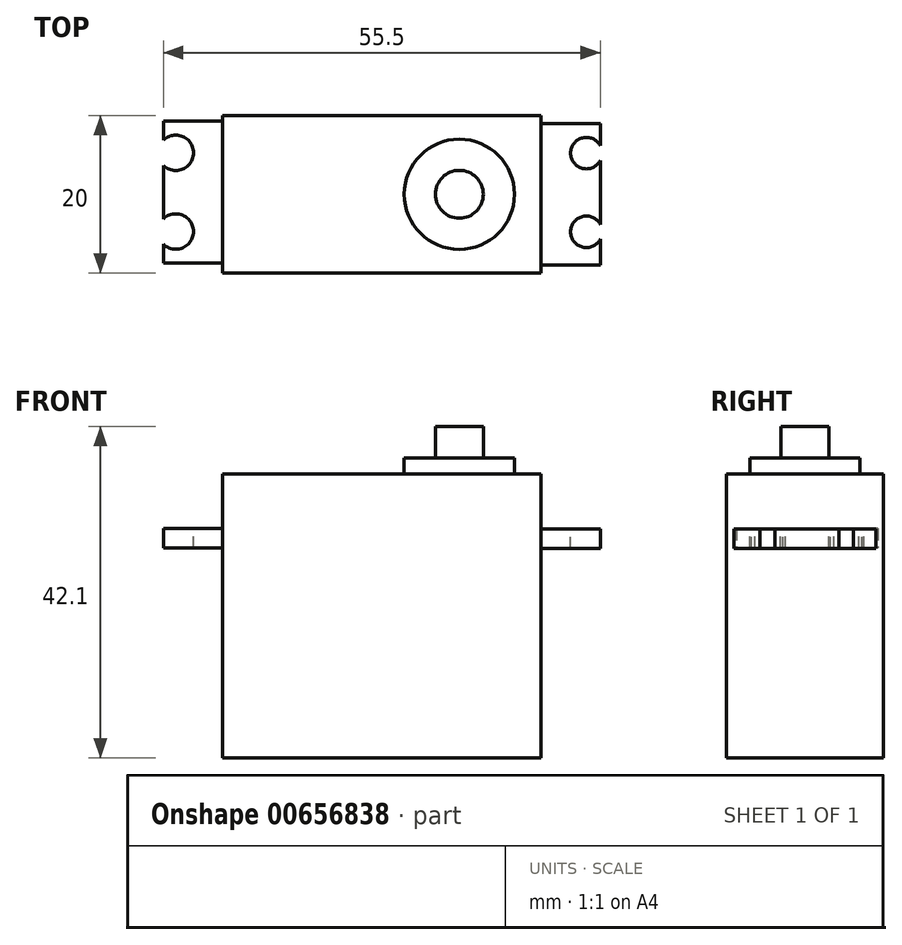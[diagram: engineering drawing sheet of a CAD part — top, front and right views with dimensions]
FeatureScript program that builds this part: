
annotation { "Feature Type Name" : "Feature", "Feature Type Description" : "" }
export const myFeature = defineFeature(function(context is Context, id is Id, definition is map)
    precondition{}
    {
        {
            var Q0;
            Q0=qCreatedBy(makeId("Top.planeOp"),FACE);
            var sketch = newSketch(context, id + "F0", { "sketchPlane" : qUnion([Q0])});
            skLineSegment(sketch, "E0.bottom", {"start": v(-74.66, 58.2) * mm, "end": v(-34.16, 58.2) * mm});
            skLineSegment(sketch, "E0.top", {"start": v(-74.66, 38.2) * mm, "end": v(-34.16, 38.2) * mm});
            skLineSegment(sketch, "E0.left", {"start": v(-74.66, 58.2) * mm, "end": v(-74.66, 38.2) * mm});
            skLineSegment(sketch, "E0.right", {"start": v(-34.16, 58.2) * mm, "end": v(-34.16, 38.2) * mm});
            skSolve(sketch);
        }
        {
            var Q0;
            Q0 = qSketchRegion(id + "F0", true);
            extrude(context, id + "F1", {"entities" : qUnion([Q0]), "depth" : 36.1 * mm, "offsetDistance" : 25 * mm});
        }
        {
            var Q0;
            Q0=makeQuery(id+"F1.opExtrude","SWEPT_FACE",FACE,{"disambiguationData":[OSD([sQuery(id+"F0.wireOp",EDGE,"E0.right")])]});
            var sketch = newSketch(context, id + "F2", { "sketchPlane" : qUnion([Q0])});
            skLineSegment(sketch, "E1.bottom", {"start": v(39.2, 29.1) * mm, "end": v(57.2, 29.1) * mm});
            skLineSegment(sketch, "E1.top", {"start": v(39.2, 26.6) * mm, "end": v(57.2, 26.6) * mm});
            skLineSegment(sketch, "E1.left", {"start": v(39.2, 29.1) * mm, "end": v(39.2, 26.6) * mm});
            skLineSegment(sketch, "E1.right", {"start": v(57.2, 29.1) * mm, "end": v(57.2, 26.6) * mm});
            skLineSegment(sketch, "E2", {"start": v(48.2, 36.1) * mm, "end": v(48.2, 29.1) * mm, "construction": true});
            skSolve(sketch);
        }
        {
            var Q0;
            Q0=makeQuery(id+"F2.imprint","IMPRINT",FACE,{"disambiguationData":[TD([[makeQuery(id+"F2.imprint","IMPRINT",EDGE,{"derivedFrom":sQuery(id+"F2.wireOp",EDGE,"E1.bottom")}),-1.0]])]});
            extrude(context, id + "F3", {"entities" : qUnion([Q0]), "operationType" : NewBodyOperationType.ADD, "depth" : 7.5 * mm, "offsetDistance" : 25 * mm});
        }
        {
            var Q0;
            Q0=makeQuery(id+"F1.opExtrude","SWEPT_FACE",FACE,{"disambiguationData":[OSD([sQuery(id+"F0.wireOp",EDGE,"E0.left")])]});
            var sketch = newSketch(context, id + "F4", { "sketchPlane" : qUnion([Q0])});
            skLineSegment(sketch, "E3.bottom", {"start": v(-57.47, 29.15) * mm, "end": v(-39.47, 29.15) * mm});
            skLineSegment(sketch, "E3.top", {"start": v(-57.47, 26.65) * mm, "end": v(-39.47, 26.65) * mm});
            skLineSegment(sketch, "E3.left", {"start": v(-57.47, 29.15) * mm, "end": v(-57.47, 26.65) * mm});
            skLineSegment(sketch, "E3.right", {"start": v(-39.47, 29.15) * mm, "end": v(-39.47, 26.65) * mm});
            skSolve(sketch);
        }
        {
            var Q0;
            Q0 = qSketchRegion(id + "F4", true);
            extrude(context, id + "F5", {"entities" : qUnion([Q0]), "operationType" : NewBodyOperationType.ADD, "depth" : 7.5 * mm, "offsetDistance" : 25 * mm});
        }
        {
            var Q0;
            Q0=makeQuery(id+"F1.opExtrude","CAP_FACE",FACE,{"disambiguationData":[OSD([sQuery(id+"F0.wireOp",EDGE,"E0.bottom"),sQuery(id+"F0.wireOp",EDGE,"E0.top"),sQuery(id+"F0.wireOp",EDGE,"E0.left"),sQuery(id+"F0.wireOp",EDGE,"E0.right")])],"isStart":false});
            var sketch = newSketch(context, id + "F6", { "sketchPlane" : qUnion([Q0])});
            skCircle(sketch, "E4", {"center": v(-44.56, 48.2) * mm, "radius": 7 * mm});
            skLineSegment(sketch, "E5", {"start": v(-44.56, 48.2) * mm, "end": v(-34.16, 48.2) * mm, "construction": true});
            skSolve(sketch);
        }
        {
            var Q0;
            Q0 = qSketchRegion(id + "F6", true);
            extrude(context, id + "F7", {"entities" : qUnion([Q0]), "operationType" : NewBodyOperationType.ADD, "depth" : 2 * mm, "offsetDistance" : 25 * mm});
        }
        {
            var Q0;
            Q0=makeQuery(id+"F7.opExtrude","CAP_FACE",FACE,{"disambiguationData":[OSD([sQuery(id+"F6.wireOp",EDGE,"E4")])],"isStart":false});
            var sketch = newSketch(context, id + "F8", { "sketchPlane" : qUnion([Q0])});
            skCircle(sketch, "E6", {"center": v(-44.56, 48.2) * mm, "radius": 3.04 * mm});
            skSolve(sketch);
        }
        {
            var Q0;
            Q0=makeQuery(id+"F8.imprint","IMPRINT",FACE,{"disambiguationData":[TD([[makeQuery(id+"F8.imprint","IMPRINT",EDGE,{"derivedFrom":sQuery(id+"F8.wireOp",EDGE,"E6")}),1.0]])]});
            var sketch = newSketch(context, id + "F9", { "sketchPlane" : qUnion([Q0])});
            skSolve(sketch);
        }
        {
            var Q0;
            Q0=makeQuery(id+"F9.imprint","IMPRINT",FACE,{"disambiguationData":[TD([[makeQuery(id+"F9.imprint","IMPRINT",EDGE,{"derivedFrom":makeQuery(id+"F8.imprint","IMPRINT",EDGE,{"derivedFrom":sQuery(id+"F8.wireOp",EDGE,"E6")})}),1.0]])]});
            extrude(context, id + "F10", {"entities" : qUnion([Q0]), "operationType" : NewBodyOperationType.ADD, "depth" : 4 * mm, "offsetDistance" : 25 * mm});
        }
        {
            var Q0;
            Q0=makeQuery(id+"F5.opExtrude","SWEPT_FACE",FACE,{"disambiguationData":[OSD([sQuery(id+"F4.wireOp",EDGE,"E3.bottom")])]});
            var sketch = newSketch(context, id + "F11", { "sketchPlane" : qUnion([Q0])});
            skCircle(sketch, "E7", {"center": v(-80.58, 53.47) * mm, "radius": 2.25 * mm});
            skCircle(sketch, "E8", {"center": v(-80.58, 43.47) * mm, "radius": 2.25 * mm});
            skLineSegment(sketch, "E9", {"start": v(-80.58, 53.47) * mm, "end": v(-80.58, 43.47) * mm, "construction": true});
            skLineSegment(sketch, "E10", {"start": v(-80.58, 48.47) * mm, "end": v(-74.66, 48.47) * mm, "construction": true});
            skSolve(sketch);
        }
        {
            var Q0;
            {var subQ0=sQuery(id+"F11.wireOp",EDGE,"E7");var subQ1=makeQuery(id+"F5.opExtrude","CAP_EDGE",EDGE,{"disambiguationData":[OSD([sQuery(id+"F4.wireOp",EDGE,"E3.bottom")])],"isStart":false});var subQ2=makeQuery(id+"F11.imprint","INTERSECT",VERTEX,{"disambiguationData":[OD(0.0)],"derivedFrom":[subQ1,subQ0]});Q0=makeQuery(id+"F11.imprint","IMPRINT",FACE,{"disambiguationData":[TD([[makeQuery(id+"F11.imprint","IMPRINT",EDGE,{"disambiguationData":[TD([[subQ2,1.0]])],"derivedFrom":subQ0}),1.0]])]});}
            var Q1;
            {var subQ0=sQuery(id+"F11.wireOp",EDGE,"E8");var subQ1=makeQuery(id+"F5.opExtrude","CAP_EDGE",EDGE,{"disambiguationData":[OSD([sQuery(id+"F4.wireOp",EDGE,"E3.bottom")])],"isStart":false});var subQ2=makeQuery(id+"F11.imprint","INTERSECT",VERTEX,{"disambiguationData":[OD(0.0)],"derivedFrom":[subQ1,subQ0]});Q1=makeQuery(id+"F11.imprint","IMPRINT",FACE,{"disambiguationData":[TD([[makeQuery(id+"F11.imprint","IMPRINT",EDGE,{"disambiguationData":[TD([[subQ2,-1.0]])],"derivedFrom":subQ0}),1.0]])]});}
            extrude(context, id + "F12", {"entities" : qUnion([Q0, Q1]), "operationType" : NewBodyOperationType.REMOVE, "oppositeDirection" : true, "depth" : 3 * mm, "offsetDistance" : 25 * mm});
        }
        {
            var Q0;
            Q0=makeQuery(id+"F3.opExtrude","SWEPT_FACE",FACE,{"disambiguationData":[OSD([sQuery(id+"F2.wireOp",EDGE,"E1.bottom")])]});
            var sketch = newSketch(context, id + "F13", { "sketchPlane" : qUnion([Q0])});
            skCircle(sketch, "E11", {"center": v(-28.42, 53.43) * mm, "radius": 2 * mm});
            skCircle(sketch, "E12", {"center": v(-28.42, 43.43) * mm, "radius": 2 * mm});
            skLineSegment(sketch, "E13", {"start": v(-28.42, 53.43) * mm, "end": v(-28.42, 43.43) * mm, "construction": true});
            skPoint(sketch, "E14.endSnap0", {"position": v(-34.16, 48.2) * mm});
            skLineSegment(sketch, "E15", {"start": v(-34.16, 48.2) * mm, "end": v(-28.42, 48.2) * mm, "construction": true});
            skPoint(sketch, "E15.endSnap0", {"position": v(-28.42, 48.43) * mm});
            skSolve(sketch);
        }
        {
            var Q0;
            {var subQ0=sQuery(id+"F13.wireOp",EDGE,"E11");var subQ1=makeQuery(id+"F3.opExtrude","CAP_EDGE",EDGE,{"disambiguationData":[OSD([sQuery(id+"F2.wireOp",EDGE,"E1.bottom")])],"isStart":false});var subQ2=makeQuery(id+"F13.imprint","INTERSECT",VERTEX,{"disambiguationData":[OD(0.0)],"derivedFrom":[subQ1,subQ0]});Q0=makeQuery(id+"F13.imprint","IMPRINT",FACE,{"disambiguationData":[TD([[makeQuery(id+"F13.imprint","IMPRINT",EDGE,{"disambiguationData":[TD([[subQ2,-1.0]])],"derivedFrom":subQ0}),1.0]])]});}
            var Q1;
            {var subQ0=sQuery(id+"F13.wireOp",EDGE,"E12");var subQ1=makeQuery(id+"F3.opExtrude","CAP_EDGE",EDGE,{"disambiguationData":[OSD([sQuery(id+"F2.wireOp",EDGE,"E1.bottom")])],"isStart":false});var subQ2=makeQuery(id+"F13.imprint","INTERSECT",VERTEX,{"disambiguationData":[OD(0.0)],"derivedFrom":[subQ1,subQ0]});Q1=makeQuery(id+"F13.imprint","IMPRINT",FACE,{"disambiguationData":[TD([[makeQuery(id+"F13.imprint","IMPRINT",EDGE,{"disambiguationData":[TD([[subQ2,1.0]])],"derivedFrom":subQ0}),1.0]])]});}
            extrude(context, id + "F14", {"entities" : qUnion([Q0, Q1]), "operationType" : NewBodyOperationType.REMOVE, "oppositeDirection" : true, "depth" : 25 * mm, "offsetDistance" : 25 * mm});
        }
    });
